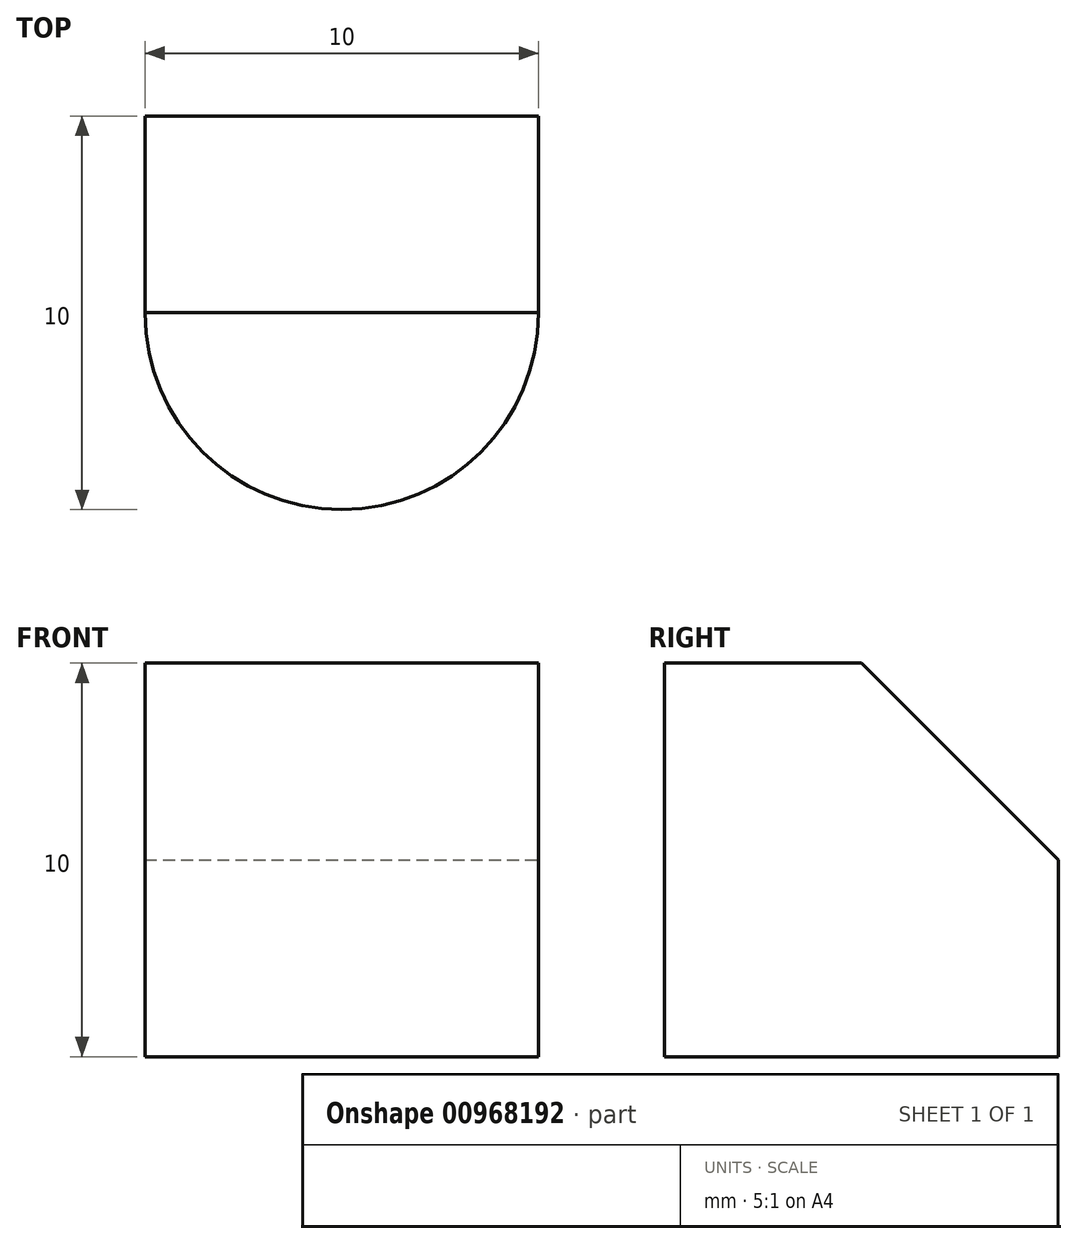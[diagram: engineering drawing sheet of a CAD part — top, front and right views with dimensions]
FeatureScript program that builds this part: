
annotation { "Feature Type Name" : "Feature", "Feature Type Description" : "" }
export const myFeature = defineFeature(function(context is Context, id is Id, definition is map)
    precondition{}
    {
        {
            var Q0;
            Q0=qCreatedBy(makeId("Top.planeOp"),FACE);
            var sketch = newSketch(context, id + "F0", { "sketchPlane" : qUnion([Q0])});
            skLineSegment(sketch, "E0.bottom", {"start": v(0, 10) * mm, "end": v(10, 10) * mm});
            skLineSegment(sketch, "E0.top", {"start": v(5, 0) * mm, "end": v(5, 0) * mm});
            skLineSegment(sketch, "E0.left", {"start": v(0, 10) * mm, "end": v(0, 5) * mm});
            skLineSegment(sketch, "E0.right", {"start": v(10, 10) * mm, "end": v(10, 5) * mm});
            skPoint(sketch, "E1.visualSharp", {"position": v(0, 0) * mm});
            skArc(sketch, "E1.filletArc", {"start": v(0, 5) * mm, "mid": v(1.46, 1.46) * mm, "end": v(5, 0) * mm});
            skPoint(sketch, "E2.visualSharp", {"position": v(10, 0) * mm});
            skArc(sketch, "E2.filletArc", {"start": v(5, 0) * mm, "mid": v(8.54, 1.46) * mm, "end": v(10, 5) * mm});
            skSolve(sketch);
        }
        {
            var Q0;
            Q0=makeQuery(id+"F0.imprint","IMPRINT",FACE,{"disambiguationData":[TD([[makeQuery(id+"F0.imprint","IMPRINT",EDGE,{"derivedFrom":sQuery(id+"F0.wireOp",EDGE,"E0.bottom")}),-1.0]])]});
            extrude(context, id + "F1", {"entities" : qUnion([Q0]), "depth" : 10 * mm, "offsetDistance" : 25 * mm});
        }
        {
            var Q0;
            Q0=makeQuery(id+"F1.opExtrude","CAP_EDGE",EDGE,{"disambiguationData":[OSD([sQuery(id+"F0.wireOp",EDGE,"E0.bottom")])],"isStart":false});
            chamfer(context, id + "F2", {"entities" : qUnion([Q0]), "width" : 5 * mm, "tangentPropagation" : true});
        }
    });
